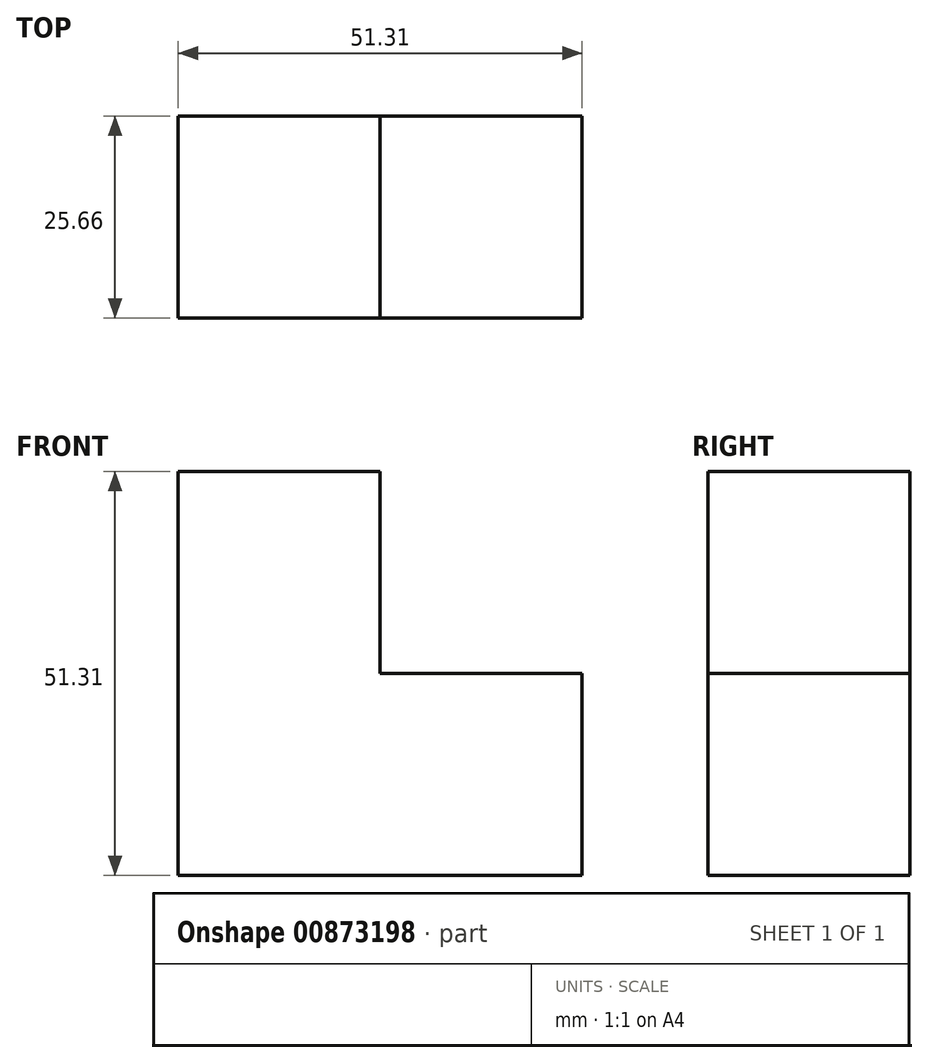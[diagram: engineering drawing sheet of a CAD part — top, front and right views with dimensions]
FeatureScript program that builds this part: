
annotation { "Feature Type Name" : "Feature", "Feature Type Description" : "" }
export const myFeature = defineFeature(function(context is Context, id is Id, definition is map)
    precondition{}
    {
        {
            var Q0;
            Q0=qCreatedBy(makeId("Front.planeOp"),FACE);
            var sketch = newSketch(context, id + "F0", { "sketchPlane" : qUnion([Q0])});
            skLineSegment(sketch, "E0", {"start": v(-51.3, -34.8) * mm, "end": v(0, -34.8) * mm});
            skLineSegment(sketch, "E1", {"start": v(0, -34.8) * mm, "end": v(0, -9.15) * mm});
            skLineSegment(sketch, "E2", {"start": v(0, -9.15) * mm, "end": v(-25.65, -9.15) * mm});
            skLineSegment(sketch, "E3", {"start": v(-25.65, -9.15) * mm, "end": v(-25.65, 16.5) * mm});
            skLineSegment(sketch, "E4", {"start": v(-25.65, 16.5) * mm, "end": v(-51.3, 16.5) * mm});
            skLineSegment(sketch, "E5", {"start": v(-51.3, 16.5) * mm, "end": v(-51.3, -34.8) * mm});
            skSolve(sketch);
        }
        {
            var Q0;
            Q0=makeQuery(id+"F0.imprint","IMPRINT",FACE,{"disambiguationData":[TD([[makeQuery(id+"F0.imprint","IMPRINT",EDGE,{"derivedFrom":sQuery(id+"F0.wireOp",EDGE,"E0")}),1.0]])]});
            extrude(context, id + "F1", {"entities" : qUnion([Q0]), "endBound" : BoundingType.SYMMETRIC, "depth" : 25.65 * mm, "offsetDistance" : 25.4 * mm});
        }
    });
